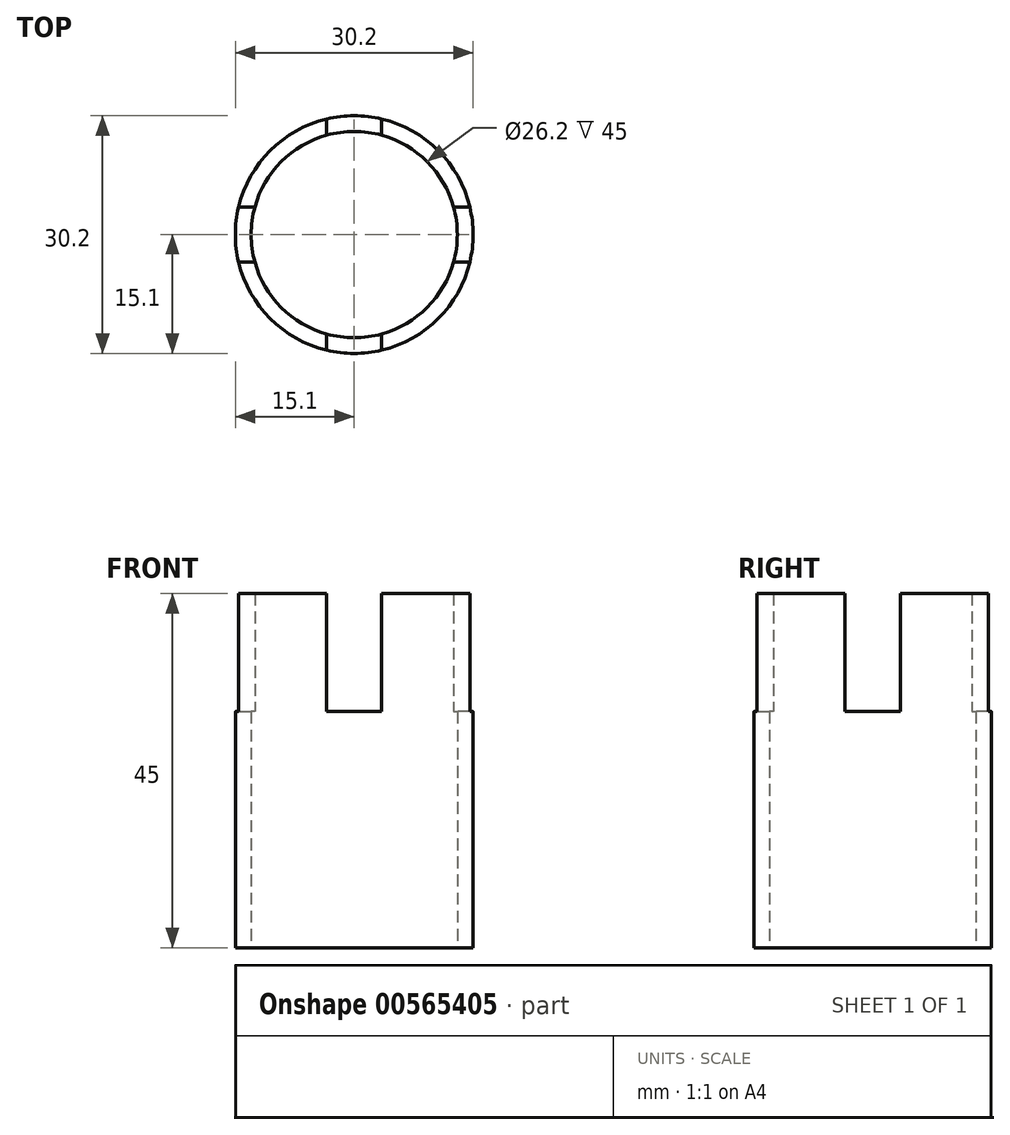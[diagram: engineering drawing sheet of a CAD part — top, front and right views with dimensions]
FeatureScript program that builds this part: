
annotation { "Feature Type Name" : "Feature", "Feature Type Description" : "" }
export const myFeature = defineFeature(function(context is Context, id is Id, definition is map)
    precondition{}
    {
        {
            var Q0;
            Q0=qCreatedBy(makeId("Top.planeOp"),FACE);
            var sketch = newSketch(context, id + "F0", { "sketchPlane" : qUnion([Q0])});
            skCircle(sketch, "E0", {"center": v(0, 0) * mm, "radius": 15.1 * mm});
            skCircle(sketch, "E1", {"center": v(0, 0) * mm, "radius": 13.1 * mm});
            skSolve(sketch);
        }
        {
            var Q0;
            Q0 = qSketchRegion(id + "F0", true);
            extrude(context, id + "F1", {"entities" : qUnion([Q0]), "depth" : 45 * mm, "offsetDistance" : 25 * mm});
        }
        {
            var Q0;
            Q0=qCreatedBy(makeId("Front.planeOp"),FACE);
            var sketch = newSketch(context, id + "F2", { "sketchPlane" : qUnion([Q0])});
            skLineSegment(sketch, "E2.bottom", {"start": v(-3.5, 45) * mm, "end": v(3.5, 45) * mm});
            skLineSegment(sketch, "E2.top", {"start": v(-3.5, 30) * mm, "end": v(3.5, 30) * mm});
            skLineSegment(sketch, "E2.left", {"start": v(-3.5, 45) * mm, "end": v(-3.5, 30) * mm});
            skLineSegment(sketch, "E2.right", {"start": v(3.5, 45) * mm, "end": v(3.5, 30) * mm});
            skPoint(sketch, "E3", {"position": v(0, 45) * mm});
            skSolve(sketch);
        }
        {
            var Q0;
            Q0 = qSketchRegion(id + "F2", true);
            extrude(context, id + "F3", {"entities" : qUnion([Q0]), "operationType" : NewBodyOperationType.REMOVE, "oppositeDirection" : true, "depth" : 25 * mm, "offsetDistance" : 25 * mm});
        }
        {
            var Q0;
            Q0 = qSketchRegion(id + "F2", true);
            extrude(context, id + "F4", {"entities" : qUnion([Q0]), "operationType" : NewBodyOperationType.REMOVE, "depth" : 25 * mm, "offsetDistance" : 25 * mm});
        }
        {
            var Q0;
            Q0=qCreatedBy(makeId("Right.planeOp"),FACE);
            var sketch = newSketch(context, id + "F5", { "sketchPlane" : qUnion([Q0])});
            skLineSegment(sketch, "E4.bottom", {"start": v(3.5, 45) * mm, "end": v(-3.5, 45) * mm});
            skLineSegment(sketch, "E4.top", {"start": v(3.5, 30) * mm, "end": v(-3.5, 30) * mm});
            skLineSegment(sketch, "E4.left", {"start": v(3.5, 45) * mm, "end": v(3.5, 30) * mm});
            skLineSegment(sketch, "E4.right", {"start": v(-3.5, 45) * mm, "end": v(-3.5, 30) * mm});
            skPoint(sketch, "E5", {"position": v(0, 45) * mm});
            skSolve(sketch);
        }
        {
            var Q0;
            Q0 = qSketchRegion(id + "F5", true);
            extrude(context, id + "F6", {"entities" : qUnion([Q0]), "operationType" : NewBodyOperationType.REMOVE, "oppositeDirection" : true, "depth" : 25 * mm, "offsetDistance" : 25 * mm});
        }
        {
            var Q0;
            Q0 = qSketchRegion(id + "F5", true);
            extrude(context, id + "F7", {"entities" : qUnion([Q0]), "operationType" : NewBodyOperationType.REMOVE, "depth" : 25 * mm, "offsetDistance" : 25 * mm});
        }
    });
